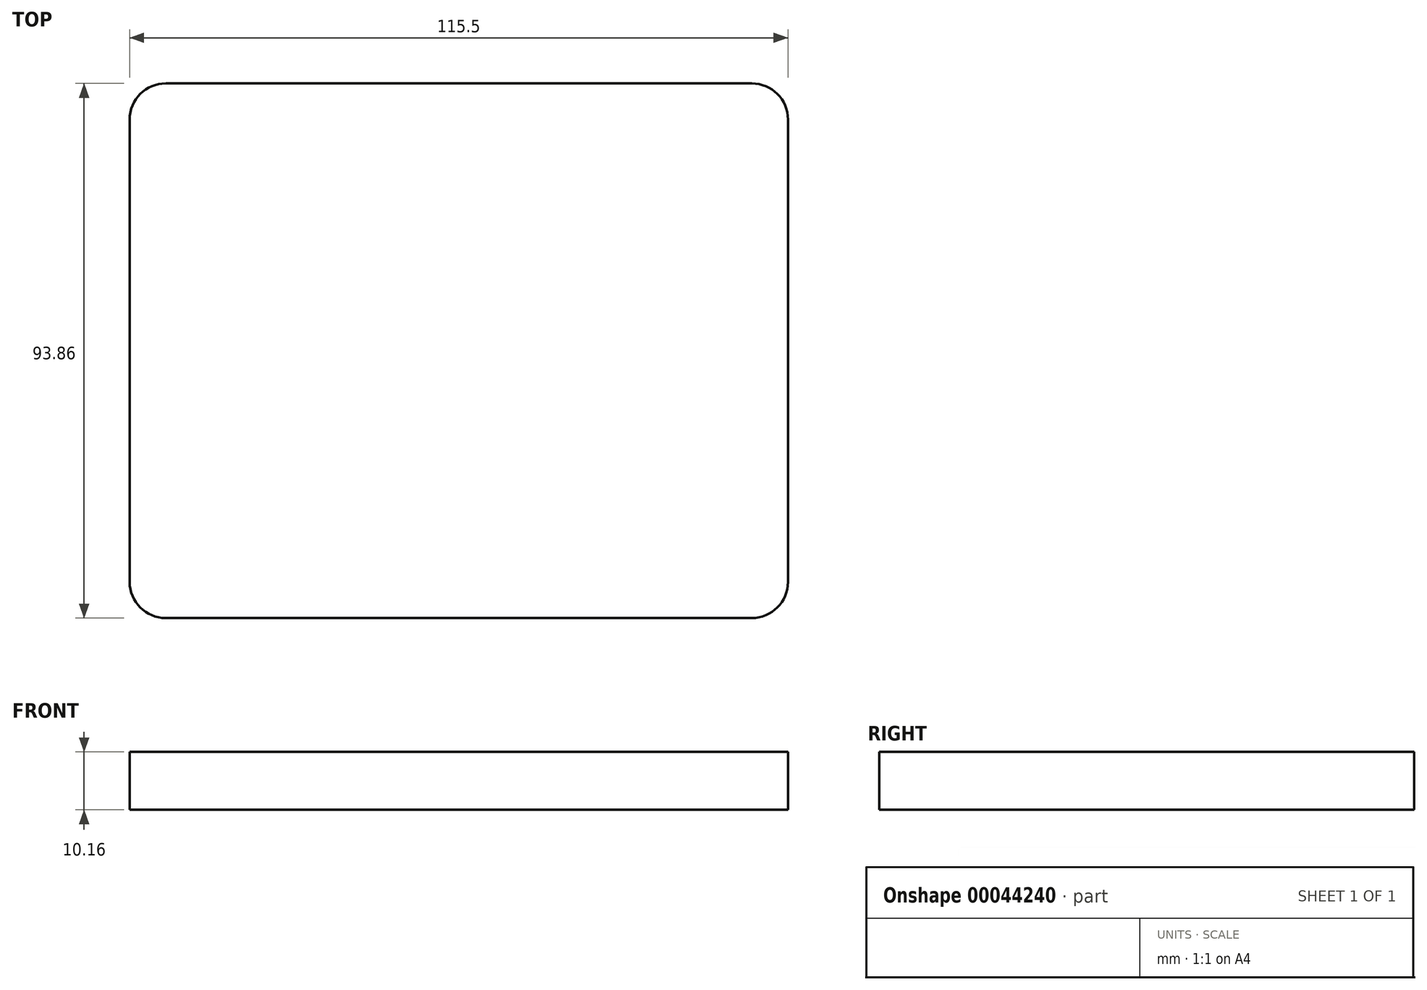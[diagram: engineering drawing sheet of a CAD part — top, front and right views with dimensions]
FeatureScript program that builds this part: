
annotation { "Feature Type Name" : "Feature", "Feature Type Description" : "" }
export const myFeature = defineFeature(function(context is Context, id is Id, definition is map)
    precondition{}
    {
        {
            var Q0;
            Q0=qCreatedBy(makeId("Top.planeOp"),FACE);
            var sketch = newSketch(context, id + "F0", { "sketchPlane" : qUnion([Q0])});
            skLineSegment(sketch, "E0.rect.bottom", {"start": v(51.4, -46.93) * mm, "end": v(-51.4, -46.93) * mm});
            skLineSegment(sketch, "E0.rect.top", {"start": v(51.4, 46.93) * mm, "end": v(-51.4, 46.93) * mm});
            skLineSegment(sketch, "E0.rect.left", {"start": v(57.75, -40.58) * mm, "end": v(57.75, 40.58) * mm});
            skLineSegment(sketch, "E0.rect.right", {"start": v(-57.75, -40.58) * mm, "end": v(-57.75, 40.58) * mm});
            skPoint(sketch, "E0.rect.middle", {"position": v(0, 0) * mm});
            skPoint(sketch, "E1.visualSharp", {"position": v(-57.75, -46.93) * mm});
            skArc(sketch, "E1.filletArc", {"start": v(-57.75, -40.58) * mm, "mid": v(-55.9, -45.07) * mm, "end": v(-51.4, -46.93) * mm});
            skPoint(sketch, "E2.visualSharp", {"position": v(-57.75, 46.93) * mm});
            skArc(sketch, "E2.filletArc", {"start": v(-51.4, 46.93) * mm, "mid": v(-55.9, 45.07) * mm, "end": v(-57.75, 40.58) * mm});
            skPoint(sketch, "E3.visualSharp", {"position": v(57.75, 46.93) * mm});
            skArc(sketch, "E3.filletArc", {"start": v(57.75, 40.58) * mm, "mid": v(55.9, 45.07) * mm, "end": v(51.4, 46.93) * mm});
            skPoint(sketch, "E4.visualSharp", {"position": v(57.75, -46.93) * mm});
            skArc(sketch, "E4.filletArc", {"start": v(51.4, -46.93) * mm, "mid": v(55.9, -45.07) * mm, "end": v(57.75, -40.58) * mm});
            skSolve(sketch);
        }
        {
            var Q0;
            Q0=makeQuery(id+"F0.imprint","IMPRINT",FACE,{"disambiguationData":[TD([[makeQuery(id+"F0.imprint","IMPRINT",EDGE,{"derivedFrom":sQuery(id+"F0.wireOp",EDGE,"E0.rect.bottom")}),-1.0]])]});
            extrude(context, id + "F1", {"entities" : qUnion([Q0]), "depth" : 10.16 * mm});
        }
    });
